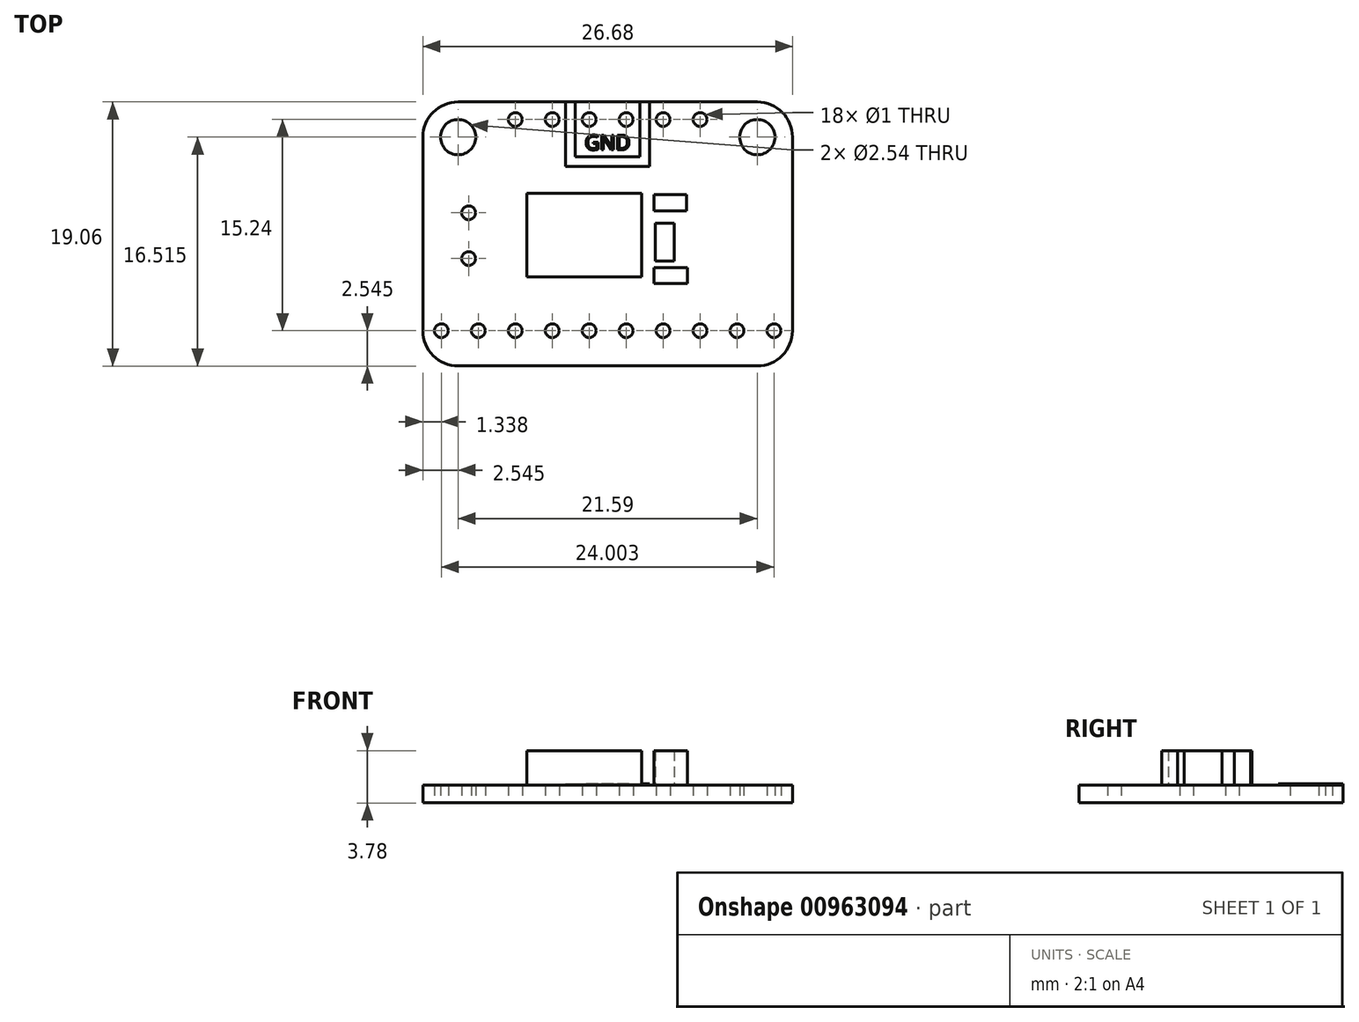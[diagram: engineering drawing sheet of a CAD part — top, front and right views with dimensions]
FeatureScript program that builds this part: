
annotation { "Feature Type Name" : "Feature", "Feature Type Description" : "" }
export const myFeature = defineFeature(function(context is Context, id is Id, definition is map)
    precondition{}
    {
        {
            var Q0;
            Q0=qCreatedBy(makeId("Top.planeOp"),FACE);
            var sketch = newSketch(context, id + "F0", { "sketchPlane" : qUnion([Q0])});
            skLineSegment(sketch, "E0.bottom", {"start": v(-10.8, 9.52) * mm, "end": v(10.8, 9.52) * mm});
            skLineSegment(sketch, "E0.top", {"start": v(-10.8, -9.52) * mm, "end": v(10.8, -9.52) * mm});
            skLineSegment(sketch, "E0.left", {"start": v(-13.33, 6.99) * mm, "end": v(-13.33, -6.98) * mm});
            skLineSegment(sketch, "E0.right", {"start": v(13.34, 6.99) * mm, "end": v(13.33, -6.98) * mm});
            skLineSegment(sketch, "E1", {"start": v(-13.34, 9.53) * mm, "end": v(13.34, -9.53) * mm, "construction": true});
            skPoint(sketch, "E2.visualSharp", {"position": v(-13.33, 9.53) * mm});
            skArc(sketch, "E2.filletArc", {"start": v(-10.8, 9.53) * mm, "mid": v(-12.6, 8.78) * mm, "end": v(-13.33, 6.99) * mm});
            skPoint(sketch, "E3.visualSharp", {"position": v(13.34, 9.53) * mm});
            skArc(sketch, "E3.filletArc", {"start": v(13.34, 6.99) * mm, "mid": v(12.6, 8.78) * mm, "end": v(10.8, 9.53) * mm});
            skPoint(sketch, "E4.visualSharp", {"position": v(13.33, -9.52) * mm});
            skArc(sketch, "E4.filletArc", {"start": v(10.8, -9.52) * mm, "mid": v(12.6, -8.78) * mm, "end": v(13.33, -6.98) * mm});
            skPoint(sketch, "E5.visualSharp", {"position": v(-13.33, -9.52) * mm});
            skArc(sketch, "E5.filletArc", {"start": v(-13.33, -6.98) * mm, "mid": v(-12.6, -8.78) * mm, "end": v(-10.8, -9.52) * mm});
            skCircle(sketch, "E6", {"center": v(-10.8, 6.99) * mm, "radius": 1.27 * mm});
            skCircle(sketch, "E7", {"center": v(10.8, 6.99) * mm, "radius": 1.27 * mm});
            skLineSegment(sketch, "E8", {"start": v(0, 0) * mm, "end": v(0, 8.25) * mm, "construction": true});
            skCircle(sketch, "E9", {"center": v(-1.33, 8.25) * mm, "radius": 0.5 * mm});
            skCircle(sketch, "E10", {"center": v(1.33, 8.25) * mm, "radius": 0.5 * mm});
            skCircle(sketch, "E11", {"center": v(4, 8.25) * mm, "radius": 0.5 * mm});
            skCircle(sketch, "E12", {"center": v(6.67, 8.25) * mm, "radius": 0.5 * mm});
            skCircle(sketch, "E13", {"center": v(-4, 8.25) * mm, "radius": 0.5 * mm});
            skCircle(sketch, "E14", {"center": v(-6.67, 8.25) * mm, "radius": 0.5 * mm});
            skLineSegment(sketch, "E15", {"start": v(1.33, 8.25) * mm, "end": v(-1.33, 8.25) * mm, "construction": true});
            skLineSegment(sketch, "E16", {"start": v(-1.33, 8.25) * mm, "end": v(-4, 8.25) * mm, "construction": true});
            skLineSegment(sketch, "E17", {"start": v(-4, 8.25) * mm, "end": v(-6.67, 8.25) * mm, "construction": true});
            skLineSegment(sketch, "E18", {"start": v(1.33, 8.25) * mm, "end": v(4, 8.25) * mm, "construction": true});
            skLineSegment(sketch, "E19", {"start": v(4, 8.25) * mm, "end": v(6.67, 8.25) * mm, "construction": true});
            skLineSegment(sketch, "E20", {"start": v(1.33, -6.99) * mm, "end": v(-1.33, -6.99) * mm, "construction": true});
            skLineSegment(sketch, "E21", {"start": v(-1.33, -6.99) * mm, "end": v(-4, -6.99) * mm, "construction": true});
            skLineSegment(sketch, "E22", {"start": v(-4, -6.99) * mm, "end": v(-6.67, -6.99) * mm, "construction": true});
            skLineSegment(sketch, "E23", {"start": v(-6.67, -6.99) * mm, "end": v(-9.33, -6.99) * mm, "construction": true});
            skLineSegment(sketch, "E24", {"start": v(-9.33, -6.99) * mm, "end": v(-12, -6.99) * mm, "construction": true});
            skLineSegment(sketch, "E25", {"start": v(1.33, -6.99) * mm, "end": v(4, -6.99) * mm, "construction": true});
            skLineSegment(sketch, "E26", {"start": v(4, -6.99) * mm, "end": v(6.67, -6.99) * mm, "construction": true});
            skLineSegment(sketch, "E27", {"start": v(6.67, -6.99) * mm, "end": v(9.33, -6.99) * mm, "construction": true});
            skLineSegment(sketch, "E28", {"start": v(9.33, -6.99) * mm, "end": v(12, -6.99) * mm, "construction": true});
            skCircle(sketch, "E29", {"center": v(-12, -6.99) * mm, "radius": 0.5 * mm});
            skCircle(sketch, "E30", {"center": v(-9.33, -6.99) * mm, "radius": 0.5 * mm});
            skCircle(sketch, "E31", {"center": v(-6.67, -6.99) * mm, "radius": 0.5 * mm});
            skCircle(sketch, "E32", {"center": v(-4, -6.99) * mm, "radius": 0.5 * mm});
            skCircle(sketch, "E33", {"center": v(-1.33, -6.99) * mm, "radius": 0.5 * mm});
            skCircle(sketch, "E34", {"center": v(1.33, -6.99) * mm, "radius": 0.5 * mm});
            skCircle(sketch, "E35", {"center": v(4, -6.99) * mm, "radius": 0.5 * mm});
            skCircle(sketch, "E36", {"center": v(6.67, -6.99) * mm, "radius": 0.5 * mm});
            skCircle(sketch, "E37", {"center": v(9.33, -6.99) * mm, "radius": 0.5 * mm});
            skCircle(sketch, "E38", {"center": v(12, -6.99) * mm, "radius": 0.5 * mm});
            skCircle(sketch, "E39", {"center": v(-10.03, -1.78) * mm, "radius": 0.5 * mm});
            skCircle(sketch, "E40", {"center": v(-10.03, 1.52) * mm, "radius": 0.5 * mm});
            skLineSegment(sketch, "E41", {"start": v(-10.03, -1.78) * mm, "end": v(-10.03, 1.52) * mm, "construction": true});
            skLineSegment(sketch, "E42", {"start": v(-10.03, -0.13) * mm, "end": v(-15.36, -0.13) * mm, "construction": true});
            skSolve(sketch);
        }
        {
            var Q0;
            Q0 = qSketchRegion(id + "F0", true);
            extrude(context, id + "F1", {"entities" : qUnion([Q0]), "depth" : (0.05 * 25.4) * mm, "offsetDistance" : 25 * mm, "symmetric" : true});
        }
        {
            var Q0;
            Q0=makeQuery(id+"F1.opExtrude","CAP_FACE",FACE,{"disambiguationData":[OSD([sQuery(id+"F0.wireOp",EDGE,"E0.bottom"),sQuery(id+"F0.wireOp",EDGE,"E0.top"),sQuery(id+"F0.wireOp",EDGE,"E0.left"),sQuery(id+"F0.wireOp",EDGE,"E0.right"),sQuery(id+"F0.wireOp",EDGE,"E2.filletArc"),sQuery(id+"F0.wireOp",EDGE,"E3.filletArc"),sQuery(id+"F0.wireOp",EDGE,"E4.filletArc"),sQuery(id+"F0.wireOp",EDGE,"E5.filletArc"),sQuery(id+"F0.wireOp",EDGE,"E6"),sQuery(id+"F0.wireOp",EDGE,"E7"),sQuery(id+"F0.wireOp",EDGE,"E9"),sQuery(id+"F0.wireOp",EDGE,"E10"),sQuery(id+"F0.wireOp",EDGE,"E11"),sQuery(id+"F0.wireOp",EDGE,"E12"),sQuery(id+"F0.wireOp",EDGE,"E13"),sQuery(id+"F0.wireOp",EDGE,"E14"),sQuery(id+"F0.wireOp",EDGE,"E29"),sQuery(id+"F0.wireOp",EDGE,"E30"),sQuery(id+"F0.wireOp",EDGE,"E31"),sQuery(id+"F0.wireOp",EDGE,"E32"),sQuery(id+"F0.wireOp",EDGE,"E33"),sQuery(id+"F0.wireOp",EDGE,"E34"),sQuery(id+"F0.wireOp",EDGE,"E35"),sQuery(id+"F0.wireOp",EDGE,"E36"),sQuery(id+"F0.wireOp",EDGE,"E37"),sQuery(id+"F0.wireOp",EDGE,"E38"),sQuery(id+"F0.wireOp",EDGE,"E39"),sQuery(id+"F0.wireOp",EDGE,"E40")])],"isStart":false});
            var sketch = newSketch(context, id + "F2", { "sketchPlane" : qUnion([Q0])});
            skLineSegment(sketch, "E43.top", {"start": v(-2.33, 5.55) * mm, "end": v(2.33, 5.55) * mm});
            skLineSegment(sketch, "E43.left", {"start": v(-2.33, 9.52) * mm, "end": v(-2.33, 5.55) * mm});
            skLineSegment(sketch, "E43.right", {"start": v(2.33, 9.52) * mm, "end": v(2.33, 5.55) * mm});
            skLineSegment(sketch, "E44.bottom", {"start": v(-3.03, 9.52) * mm, "end": v(-2.33, 9.52) * mm});
            skLineSegment(sketch, "E44.top", {"start": v(-3.03, 4.85) * mm, "end": v(3.03, 4.85) * mm});
            skLineSegment(sketch, "E44.left", {"start": v(-3.03, 9.52) * mm, "end": v(-3.03, 4.85) * mm});
            skLineSegment(sketch, "E44.right", {"start": v(3.03, 9.52) * mm, "end": v(3.03, 4.85) * mm});
            skLineSegment(sketch, "E45", {"start": v(-1.33, 8.25) * mm, "end": v(1.33, 8.25) * mm, "construction": true});
            skLineSegment(sketch, "E46.trimOffspring", {"start": v(2.33, 9.52) * mm, "end": v(3.03, 9.52) * mm});
            skText(sketch, "E47", { "text": "GND", "fontName": "OpenSans-Regular.ttf"});
            const initialGuessF2  = {"E47": [-0.00165, 0.00607, 1, 0, 0.00107]};
            skSetInitialGuess(sketch, initialGuessF2);
            skSolve(sketch);
        }
        {
            var Q0;
            Q0 = qSketchRegion(id + "F2", true);
            extrude(context, id + "F3", {"entities" : qUnion([Q0]), "operationType" : NewBodyOperationType.ADD, "depth" : 0.1 * mm, "offsetDistance" : 25 * mm});
        }
        {
            var Q0;
            {var subQ0=sQuery(id+"F0.wireOp",EDGE,"E36");var subQ1=sQuery(id+"F0.wireOp",EDGE,"E35");var subQ2=sQuery(id+"F0.wireOp",EDGE,"E33");var subQ3=sQuery(id+"F0.wireOp",EDGE,"E32");var subQ4=sQuery(id+"F0.wireOp",EDGE,"E31");var subQ5=sQuery(id+"F0.wireOp",EDGE,"E30");var subQ6=sQuery(id+"F0.wireOp",EDGE,"E29");var subQ7=sQuery(id+"F0.wireOp",EDGE,"E14");var subQ8=sQuery(id+"F0.wireOp",EDGE,"E13");var subQ9=sQuery(id+"F0.wireOp",EDGE,"E12");var subQ10=sQuery(id+"F0.wireOp",EDGE,"E11");var subQ11=sQuery(id+"F0.wireOp",EDGE,"E0.left");var subQ12=sQuery(id+"F0.wireOp",EDGE,"E0.top");var subQ13=sQuery(id+"F0.wireOp",EDGE,"E0.right");var subQ14=sQuery(id+"F0.wireOp",EDGE,"E34");var subQ15=sQuery(id+"F0.wireOp",EDGE,"E0.bottom");var subQ16=sQuery(id+"F0.wireOp",EDGE,"E7");var subQ17=sQuery(id+"F0.wireOp",EDGE,"E2.filletArc");var subQ18=sQuery(id+"F0.wireOp",EDGE,"E3.filletArc");var subQ19=sQuery(id+"F0.wireOp",EDGE,"E4.filletArc");var subQ20=sQuery(id+"F0.wireOp",EDGE,"E5.filletArc");var subQ21=sQuery(id+"F0.wireOp",EDGE,"E6");var subQ22=sQuery(id+"F0.wireOp",EDGE,"E37");var subQ23=sQuery(id+"F0.wireOp",EDGE,"E38");var subQ24=sQuery(id+"F0.wireOp",EDGE,"E39");var subQ25=sQuery(id+"F0.wireOp",EDGE,"E40");Q0=makeQuery(id+"F3.boolean.opBoolean","SPLIT",FACE,{"disambiguationData":[TD([makeQuery(id+"F1.opExtrude","SWEPT_FACE",FACE,{"disambiguationData":[OSD([subQ12])]})])],"derivedFrom":makeQuery(id+"F1.opExtrude","CAP_FACE",FACE,{"disambiguationData":[OSD([subQ15,subQ12,subQ11,subQ13,subQ17,subQ18,subQ19,subQ20,subQ21,subQ16,sQuery(id+"F0.wireOp",EDGE,"E9"),sQuery(id+"F0.wireOp",EDGE,"E10"),subQ10,subQ9,subQ8,subQ7,subQ6,subQ5,subQ4,subQ3,subQ2,subQ14,subQ1,subQ0,subQ22,subQ23,subQ24,subQ25])],"isStart":false})});}
            var sketch = newSketch(context, id + "F4", { "sketchPlane" : qUnion([Q0])});
            skLineSegment(sketch, "E48.bottom", {"start": v(-5.84, -3.08) * mm, "end": v(2.45, -3.08) * mm});
            skLineSegment(sketch, "E48.top", {"start": v(-5.84, 2.93) * mm, "end": v(2.45, 2.93) * mm});
            skLineSegment(sketch, "E48.left", {"start": v(-5.84, -3.08) * mm, "end": v(-5.84, 2.93) * mm});
            skLineSegment(sketch, "E48.right", {"start": v(2.45, -3.08) * mm, "end": v(2.45, 2.93) * mm});
            skLineSegment(sketch, "E49.bottom", {"start": v(3.43, -1.95) * mm, "end": v(4.8, -1.95) * mm});
            skLineSegment(sketch, "E49.top", {"start": v(3.43, 0.78) * mm, "end": v(4.8, 0.78) * mm});
            skLineSegment(sketch, "E49.left", {"start": v(3.43, -1.95) * mm, "end": v(3.43, 0.78) * mm});
            skLineSegment(sketch, "E49.right", {"start": v(4.8, -1.95) * mm, "end": v(4.8, 0.78) * mm});
            skLineSegment(sketch, "E50.bottom", {"start": v(3.35, 1.67) * mm, "end": v(5.7, 1.67) * mm});
            skLineSegment(sketch, "E50.top", {"start": v(3.35, 2.85) * mm, "end": v(5.7, 2.85) * mm});
            skLineSegment(sketch, "E50.left", {"start": v(3.35, 1.67) * mm, "end": v(3.35, 2.85) * mm});
            skLineSegment(sketch, "E50.right", {"start": v(5.7, 1.67) * mm, "end": v(5.7, 2.85) * mm});
            skLineSegment(sketch, "E51.bottom", {"start": v(3.35, -3.57) * mm, "end": v(5.75, -3.57) * mm});
            skLineSegment(sketch, "E51.top", {"start": v(3.35, -2.43) * mm, "end": v(5.75, -2.43) * mm});
            skLineSegment(sketch, "E51.left", {"start": v(3.35, -3.57) * mm, "end": v(3.35, -2.43) * mm});
            skLineSegment(sketch, "E51.right", {"start": v(5.75, -3.57) * mm, "end": v(5.75, -2.43) * mm});
            skSolve(sketch);
        }
        {
            var Q0;
            Q0 = qSketchRegion(id + "F4", true);
            extrude(context, id + "F5", {"entities" : qUnion([Q0]), "operationType" : NewBodyOperationType.ADD, "depth" : 2.5 * mm, "offsetDistance" : 25 * mm});
        }
    });
